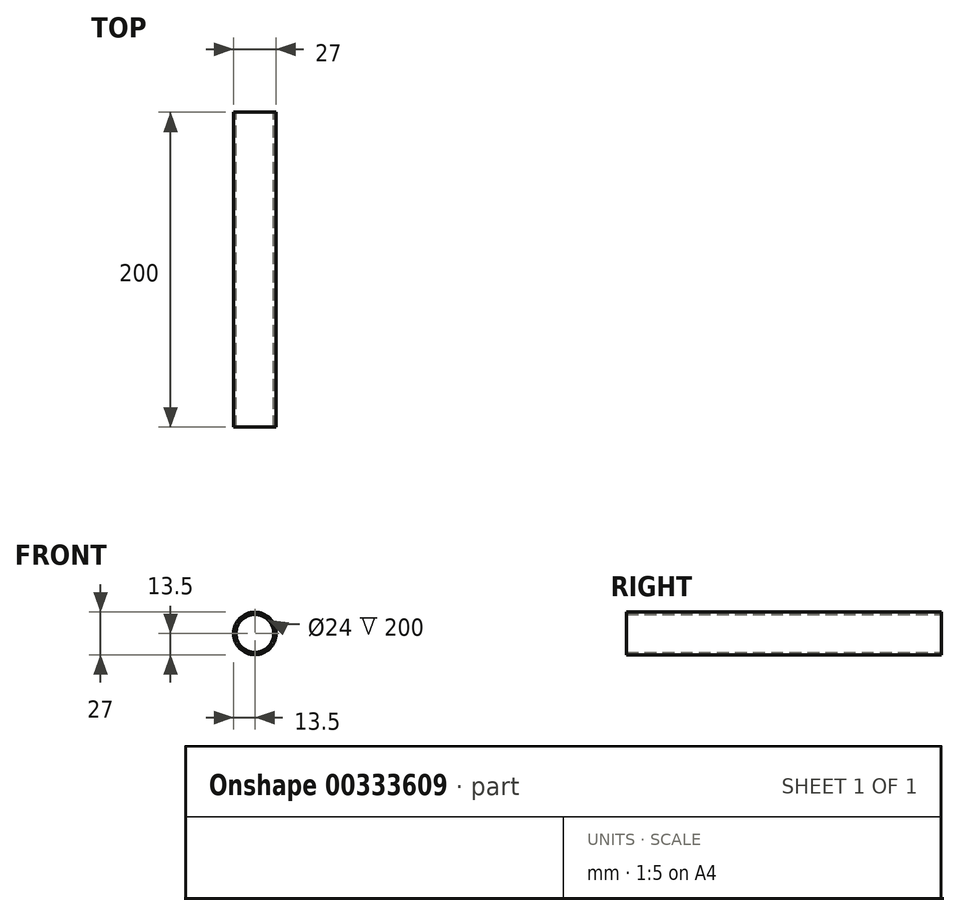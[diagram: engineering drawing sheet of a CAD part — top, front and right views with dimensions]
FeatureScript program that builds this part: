
annotation { "Feature Type Name" : "Feature", "Feature Type Description" : "" }
export const myFeature = defineFeature(function(context is Context, id is Id, definition is map)
    precondition{}
    {
        {
            var Q0;
            Q0=qCreatedBy(makeId("Front.planeOp"),FACE);
            var sketch = newSketch(context, id + "F0", { "sketchPlane" : qUnion([Q0])});
            skCircle(sketch, "E0", {"center": v(0, 0) * mm, "radius": 13.5 * mm});
            skCircle(sketch, "E1", {"center": v(0, 0) * mm, "radius": 12 * mm});
            skSolve(sketch);
        }
        {
            var Q0;
            Q0=makeQuery(id+"F0.imprint","IMPRINT",FACE,{"disambiguationData":[TD([[makeQuery(id+"F0.imprint","IMPRINT",EDGE,{"derivedFrom":sQuery(id+"F0.wireOp",EDGE,"E1")}),-1.0]])]});
            extrude(context, id + "F1", {"entities" : qUnion([Q0]), "depth" : 200 * mm});
        }
    });
